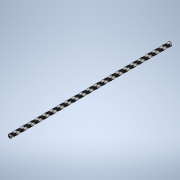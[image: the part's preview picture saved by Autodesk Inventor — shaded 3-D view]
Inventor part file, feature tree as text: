
AUTODESK INVENTOR PART (.ipt)
format: ipt  version: 2020 (Build 240168000, 168)  size: 102,400 bytes
history: native  units: in
note: dims shown in document units (in); Inventor stores cm internally (conversion verified against a paired STEP export)
features: extrude x1, sketch x1
ambient origin geometry x8: Origin, YZ Plane, XZ Plane, XY Plane, X Axis, Y Axis, Z Axis, Center Point
bodies: Solid1 (feature_tree)
feature tree (2):
  extrude  "Extrusion1"  Depth=3.2283in
  sketch  "Sketch1"  dims[d0=0.0787in d1=3.2283in d2=0.0in]
